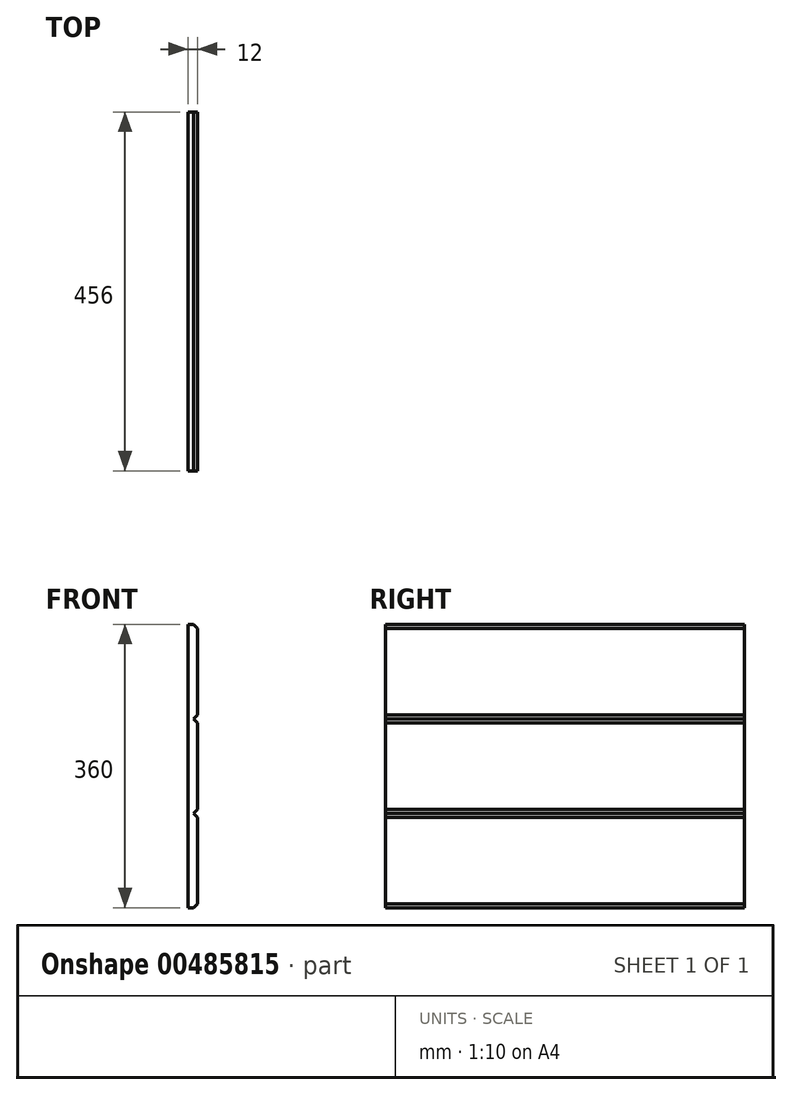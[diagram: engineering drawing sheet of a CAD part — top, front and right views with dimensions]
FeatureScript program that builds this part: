
annotation { "Feature Type Name" : "Feature", "Feature Type Description" : "" }
export const myFeature = defineFeature(function(context is Context, id is Id, definition is map)
    precondition{}
    {
        {
            var Q0;
            Q0=qCreatedBy(makeId("Right.planeOp"),FACE);
            var sketch = newSketch(context, id + "F0", { "sketchPlane" : qUnion([Q0])});
            skLineSegment(sketch, "E0.bottom", {"start": v(240, 180) * mm, "end": v(-240, 180) * mm});
            skLineSegment(sketch, "E0.top", {"start": v(240, -180) * mm, "end": v(-240, -180) * mm});
            skLineSegment(sketch, "E0.left", {"start": v(240, 180) * mm, "end": v(240, -180) * mm});
            skLineSegment(sketch, "E0.right", {"start": v(-240, 180) * mm, "end": v(-240, -180) * mm});
            skPoint(sketch, "E0.middle", {"position": v(0, 0) * mm});
            skSolve(sketch);
        }
        {
            var Q0;
            Q0=makeQuery(id+"F0.imprint","IMPRINT",FACE,{"disambiguationData":[TD([[makeQuery(id+"F0.imprint","IMPRINT",EDGE,{"derivedFrom":sQuery(id+"F0.wireOp",EDGE,"E0.bottom")}),1.0]])]});
            extrude(context, id + "F1", {"entities" : qUnion([Q0]), "depth" : 12 * mm});
        }
        {
            var Q0;
            Q0=makeQuery(id+"F1.opExtrude","SWEPT_FACE",FACE,{"disambiguationData":[OSD([sQuery(id+"F0.wireOp",EDGE,"E0.left")])]});
            var sketch = newSketch(context, id + "F2", { "sketchPlane" : qUnion([Q0])});
            skLineSegment(sketch, "E1", {"start": v(-12, -180) * mm, "end": v(-7, -180) * mm});
            skLineSegment(sketch, "E2", {"start": v(-7, -180) * mm, "end": v(-12, -175) * mm});
            skLineSegment(sketch, "E3", {"start": v(-12, -175) * mm, "end": v(-12, -180) * mm});
            skLineSegment(sketch, "E4", {"start": v(-12, -60) * mm, "end": v(-12, -65) * mm});
            skLineSegment(sketch, "E5", {"start": v(-12, -55) * mm, "end": v(-12, -60) * mm});
            skLineSegment(sketch, "E6", {"start": v(-12, -60) * mm, "end": v(-7, -60) * mm});
            skLineSegment(sketch, "E7", {"start": v(-7, -60) * mm, "end": v(-12, -65) * mm});
            skLineSegment(sketch, "E8", {"start": v(-12, -55) * mm, "end": v(-7, -60) * mm});
            skLineSegment(sketch, "E9", {"start": v(-12, 60) * mm, "end": v(-12, 55) * mm});
            skLineSegment(sketch, "E10", {"start": v(-12, 55) * mm, "end": v(-7, 60) * mm});
            skLineSegment(sketch, "E11", {"start": v(-7, 60) * mm, "end": v(-12, 65) * mm});
            skLineSegment(sketch, "E12", {"start": v(-12, 65) * mm, "end": v(-12, 60) * mm});
            skLineSegment(sketch, "E13", {"start": v(-12, 60) * mm, "end": v(-7, 60) * mm});
            skLineSegment(sketch, "E14", {"start": v(-12, 180) * mm, "end": v(-12, 175) * mm});
            skLineSegment(sketch, "E15", {"start": v(-12, 175) * mm, "end": v(-7, 180) * mm});
            skLineSegment(sketch, "E16", {"start": v(-7, 180) * mm, "end": v(-12, 180) * mm});
            skSolve(sketch);
        }
        {
            var Q0;
            Q0 = qSketchRegion(id + "F2", true);
            extrude(context, id + "F3", {"entities" : qUnion([Q0]), "operationType" : NewBodyOperationType.REMOVE, "endBound" : BoundingType.THROUGH_ALL, "oppositeDirection" : true, "depth" : 480 * mm});
        }
        {
            var Q0;
            Q0=makeQuery(id+"F1.opExtrude","SWEPT_FACE",FACE,{"disambiguationData":[OSD([sQuery(id+"F0.wireOp",EDGE,"E0.right")])]});
            extrude(context, id + "F4", {"entities" : qUnion([Q0]), "operationType" : NewBodyOperationType.REMOVE, "oppositeDirection" : true, "depth" : 24 * mm, "offsetDistance" : 25 * mm});
        }
    });
